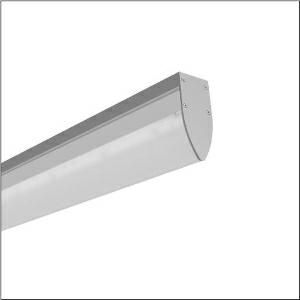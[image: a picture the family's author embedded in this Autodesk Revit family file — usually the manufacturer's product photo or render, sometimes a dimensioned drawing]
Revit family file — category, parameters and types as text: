
# Revit family: mira_r__21_td_51fr527k444a_1922
name_source: partatom
category: Lighting Fixtures
units: mm (PartAtom-declared; Revit-internal decimal feet)

## family parameters
Cut with Voids When Loaded = No
Host = Face
Light Source = No
Part Type = Normal
Room Calculation Point = No
Round Connector Dimension = Use Diameter
Shared = No

## types (1)
- Mira® 21 TD (1 x LED, 4030 lm, 27 W, 4000K)
    Apparent Load = 27 VA
    CIE Flux Codes = 40 68 87 81 100
    Color Rendering = 80
    Color Temperature = 4000K
    Default Elevation = 1800 mm
    Description = Mira® 21 TD, clean room luminaire, primary light control with reflector, primary optical cover: cover, of PMMA, frosted, light emission: direct distribution, primary light characteristic: symmetric, installation type: surface-mounted, LED, rated luminous flux: 4.030lm, luminous efficacy: 149lm/W, light colour: 840, colour temperature: 4000K, control gear: ON/OFF, with terminal, 3-pole, max. 2.5mm², mains connection: 230V, AC, 50/60Hz, rated input power: 27W, luminaire housing, of sheet steel, coated, pure white (RAL 9010), length: 1.200mm, width: 55mm, height: 120mm, protection rating (complete): IP43, insulation class (complete): insulation class I (protective earthing), certification: CE, UKCA, permissible operating ambient temperature: -5..+40°C, standard: EN 50419, packaging unit: 1 piece
    Height = 120 mm
    Lamp = 1 x LED
    Lamp Light Flux = 4030 lm
    Lamp Power = 27 W
    Lamp count = 1
    Length = 1200 mm
    Luminous efficacy = 149 lm/W
    Manufacturer = Siteco
    ModVariant = No
    Model = 51FR527K444A
    Mounting Place = Ceiling
    Mounting Type = Surface mounted
    Number of Poles = 1
    OnlyDefault = Yes
    Power Factor = 1
    Product Name = Mira® 21 TD
    Product group = clean room luminaire | ceiling mounted
    ProductGroupID = 306
    Protection Class = Protection class I
    Protection Degree = IP 43
    RLX_Detail_Level = 1
    RLX_Emergency_Light_Flux = 0 lm
    RLX_Emergency_Type = 0
    RLX_Emergency_Type_DB = No
    RlxData = <blob elided: 25137 chars, md5=617be769>
    Socket = socket
    Standby Power = 0 W
    System Light Flux = 4030 lm
    System Power = 27 W
    Type Comments = Product without accessories
    Type Image = l_1007115.jpg
    URL = http://relux.com
    VarID = ---
    Voltage = 0 V
    Weight = 0.00 kg
    Width = 55 mm

## geometry (parser evidence)
native form markers: Blend x4, Sweep x12
no freeform markers — native parametric forms only
